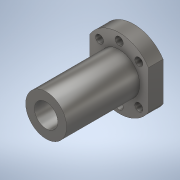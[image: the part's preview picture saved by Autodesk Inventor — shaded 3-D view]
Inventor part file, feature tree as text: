
AUTODESK INVENTOR PART (.ipt)
format: ipt  version: 2020 (Build 240168000, 168)  size: 181,760 bytes
history: native  units: mm
features: extrude x5, sketch x5, other x1, mirror x1
ambient origin geometry x8: Origin, YZ Plane, XZ Plane, XY Plane, X Axis, Y Axis, Z Axis, Center Point
bodies: Body1 (feature_tree)
feature tree (12):
  other  "Bryła1"
  extrude  "Wyciągnięcie proste1"  Depth=48.0mm
  extrude  "Wyciągnięcie proste2"  Depth=10.0mm TaperAngle=0.0deg
  extrude  "Wyciągnięcie proste3"  Depth=28.0mm
  extrude  "Wyciągnięcie proste4"  Depth=50.0mm TaperAngle=0.0deg
  extrude  "Wyciągnięcie proste5"  Depth=16.0mm
  mirror  "Odbij1"
  sketch  "Szkic1"
  sketch  "Szkic2"
  sketch  "Szkic3"
  sketch  "Szkic4"
  sketch  "Szkic5"
